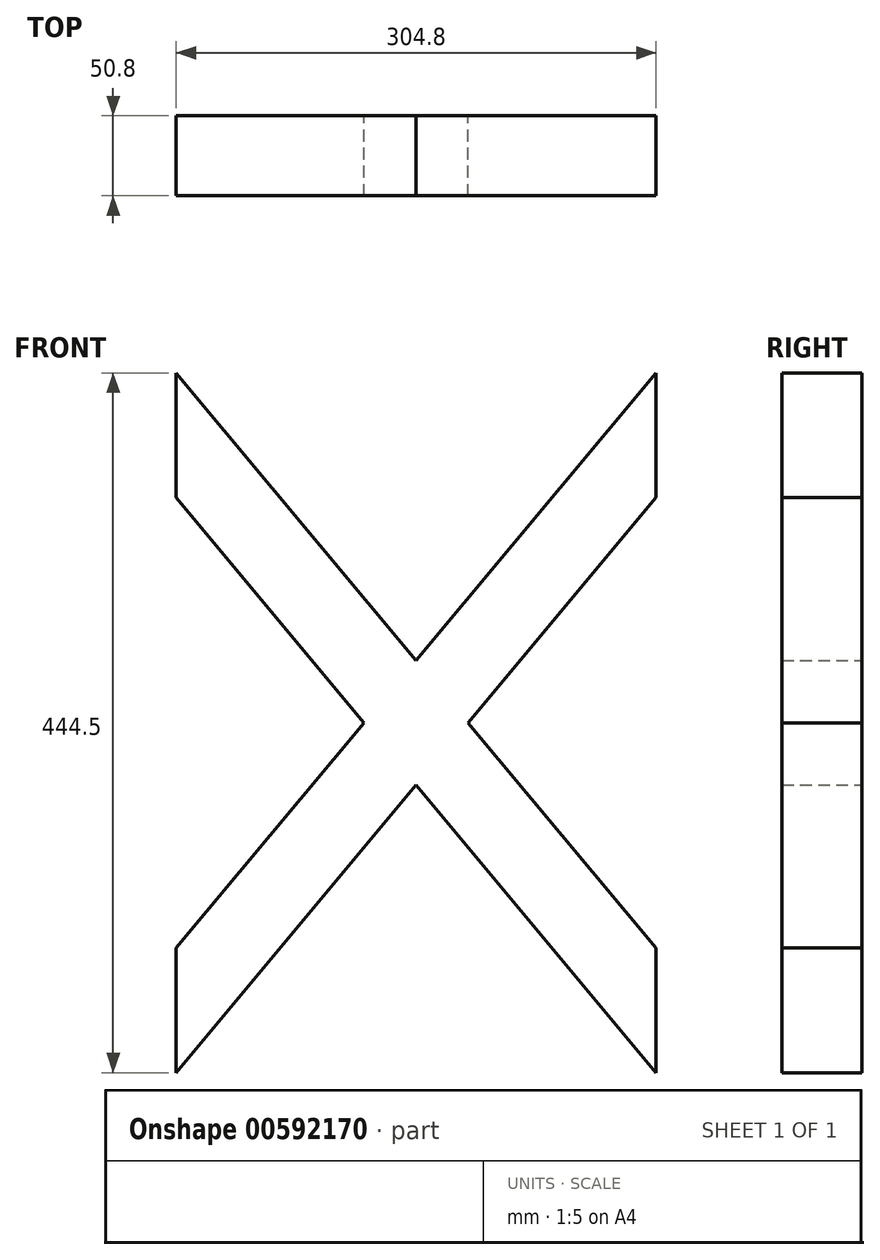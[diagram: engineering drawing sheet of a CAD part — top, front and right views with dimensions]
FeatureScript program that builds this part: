
annotation { "Feature Type Name" : "Feature", "Feature Type Description" : "" }
export const myFeature = defineFeature(function(context is Context, id is Id, definition is map)
    precondition{}
    {
        {
            var Q0;
            Q0=qCreatedBy(makeId("Front.planeOp"),FACE);
            var sketch = newSketch(context, id + "F0", { "sketchPlane" : qUnion([Q0])});
            skLineSegment(sketch, "E0.left", {"start": v(152.4, 222.25) * mm, "end": v(152.4, 142.97) * mm});
            skLineSegment(sketch, "E0.right", {"start": v(-152.4, 222.25) * mm, "end": v(-152.4, 142.97) * mm});
            skPoint(sketch, "E0.middle", {"position": v(0, 0) * mm});
            skLineSegment(sketch, "E1", {"start": v(152.4, -222.25) * mm, "end": v(0, -39.64) * mm});
            skLineSegment(sketch, "E2", {"start": v(-152.4, 142.97) * mm, "end": v(-152.4, 222.25) * mm});
            skLineSegment(sketch, "E3", {"start": v(-152.4, 222.25) * mm, "end": v(0, 39.64) * mm});
            skLineSegment(sketch, "E4", {"start": v(152.4, -142.97) * mm, "end": v(152.4, -222.25) * mm});
            skLineSegment(sketch, "E5", {"start": v(152.4, 222.25) * mm, "end": v(0, 39.64) * mm});
            skLineSegment(sketch, "E6", {"start": v(-152.4, -142.97) * mm, "end": v(-152.4, -222.25) * mm});
            skLineSegment(sketch, "E7", {"start": v(-152.4, -222.25) * mm, "end": v(0, -39.64) * mm});
            skLineSegment(sketch, "E8", {"start": v(152.4, 142.97) * mm, "end": v(152.4, 222.25) * mm});
            skLineSegment(sketch, "E9.trimOffspring", {"start": v(33.08, 0) * mm, "end": v(152.4, -142.97) * mm});
            skLineSegment(sketch, "E10.trimOffspring", {"start": v(-33.08, 0) * mm, "end": v(-152.4, -142.97) * mm});
            skLineSegment(sketch, "E11.trimOffspring", {"start": v(-33.08, 0) * mm, "end": v(-152.4, 142.97) * mm});
            skLineSegment(sketch, "E12.trimOffspring", {"start": v(33.08, 0) * mm, "end": v(152.4, 142.97) * mm});
            skSolve(sketch);
        }
        {
            var Q0;
            Q0 = qSketchRegion(id + "F0", true);
            extrude(context, id + "F1", {"entities" : qUnion([Q0]), "depth" : 50.8 * mm, "offsetDistance" : 25.4 * mm});
        }
    });
